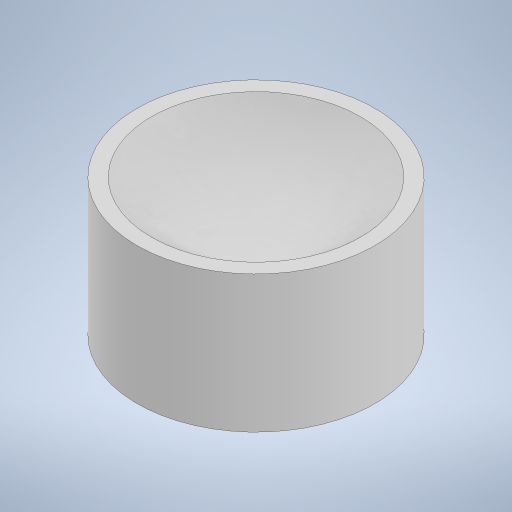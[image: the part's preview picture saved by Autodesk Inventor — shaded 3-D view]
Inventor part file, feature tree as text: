
AUTODESK INVENTOR PART (.ipt)
format: ipt  version: 2023 (Build 270158000, 158)  size: 255,488 bytes
history: native  units: mm
features: sketch x2, extrude x2, revolve x1
ambient origin geometry x8: Origin, YZ Plane, XZ Plane, XY Plane, X Axis, Y Axis, Z Axis, Center Point
bodies: Solid1 (feature_tree)
feature tree (5):
  sketch  "Sketch1"  dims[d0=28.5mm d1=15.0mm]
  extrude  "Extrusion1"  Depth=15.0mm
  extrude  "Extrusion2"  Depth=19.0mm
  revolve  "Revolution1"  [1 undecoded]
  sketch  "Sketch3"  dims[d2=9.5mm d3=33.0mm d4=6.0mm d5=0.0mm d7=1.0mm d8=40.0mm d10=360.0deg d12=5.0mm d13=0.0mm d20=2.0mm d21=8.0mm d22=19.0mm d23=360.0deg]
note: 1 required parameter value undecoded (feature->parameter linkage not recoverable at this tier; creation-order binding heuristic only, values carry confidence <= 0.55)
